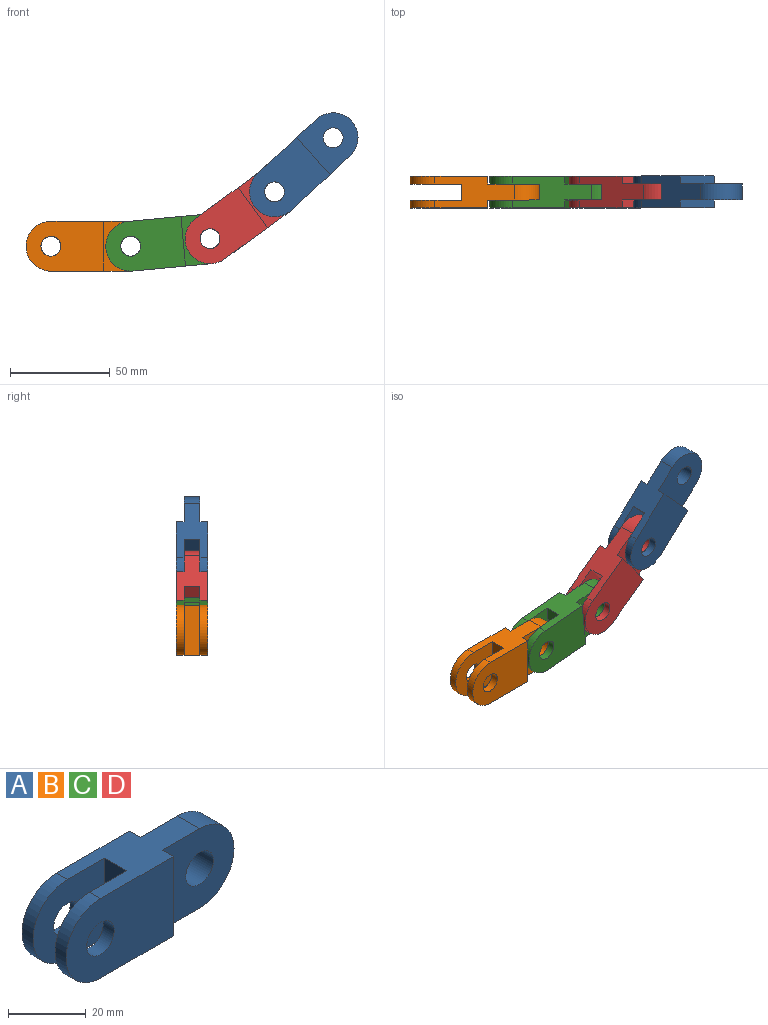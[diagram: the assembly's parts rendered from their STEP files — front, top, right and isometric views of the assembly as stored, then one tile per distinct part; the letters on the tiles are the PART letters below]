
ASSEMBLY  parts=4 mates=3
PART A: 17 faces, bbox 65x16x25 mm
  f0: plane 40x16mm, normal (0,0,-1), area 424mm2, adj f1,f2,f4,f6,f8,f9,f10,f11
  f1: cylinder r=12.5mm len=25mm, axis (0,-1,0), area 157.1mm2, adj f0,f3,f8,f14
  f2: cylinder r=12.5mm len=25mm, axis (0,-1,0), area 157.1mm2, adj f0,f3,f6,f13
  f3: plane 40x16mm, normal (0,0,1), area 424mm2, adj f1,f2,f4,f6,f8,f9,f10,f11
  f4: cylinder r=12.5mm len=25mm, axis (0,-1,0), area 314.2mm2, adj f0,f3,f9,f11
  f5: cylinder r=5mm len=10mm, axis (0,-1,0), area 125.7mm2, adj f6,f13
  f6: plane 39x25mm, normal (0,-1,0), area 829.4mm2, adj f0,f2,f3,f5,f10
  f7: cylinder r=5mm len=10mm, axis (0,-1,0), area 125.7mm2, adj f8,f14
  f8: plane 39x25mm, normal (0,1,0), area 829.4mm2, adj f0,f1,f3,f7,f12
  f9: plane 26x25mm, normal (0,-1,0), area 504.4mm2, adj f0,f3,f4,f10,f16
  f10: plane 25x4mm, normal (1,0,0), area 100mm2, adj f0,f3,f6,f9
  f11: plane 26x25mm, normal (0,1,0), area 504.4mm2, adj f0,f3,f4,f12,f16
  f12: plane 25x4mm, normal (1,0,0), area 100mm2, adj f0,f3,f8,f11
  f13: plane 26x25mm, normal (0,1,0), area 504.4mm2, adj f0,f2,f3,f5,f15
  f14: plane 26x25mm, normal (0,-1,0), area 504.4mm2, adj f0,f1,f3,f7,f15
  f15: plane 25x8mm, normal (-1,0,0), area 200mm2, adj f0,f3,f13,f14
  f16: cylinder r=5mm len=10mm, axis (0,-1,0), area 251.3mm2, adj f9,f11
PART B: same geometry as A
PART C: same geometry as A
PART D: same geometry as A
PLACE A rot(axis=(0,-1,0),42.7deg) t=(112.18,0,27.27)mm
PLACE B at identity fixed
PLACE C rot(axis=(0,-1,0),5.4deg) t=(40,0,0)mm
PLACE D rot(axis=(0,-1,0),36deg) t=(79.82,0,3.74)mm
MATE revolute D.f1 <-> C.f4  axis (0,1,0) through (79.82,-4,3.74)mm
MATE revolute A.f1 <-> D.f4  axis (0,1,0) through (112.18,-4,27.27)mm
MATE revolute C.f1 <-> B.f4  axis (0,1,0) through (40,-4,0)mm
